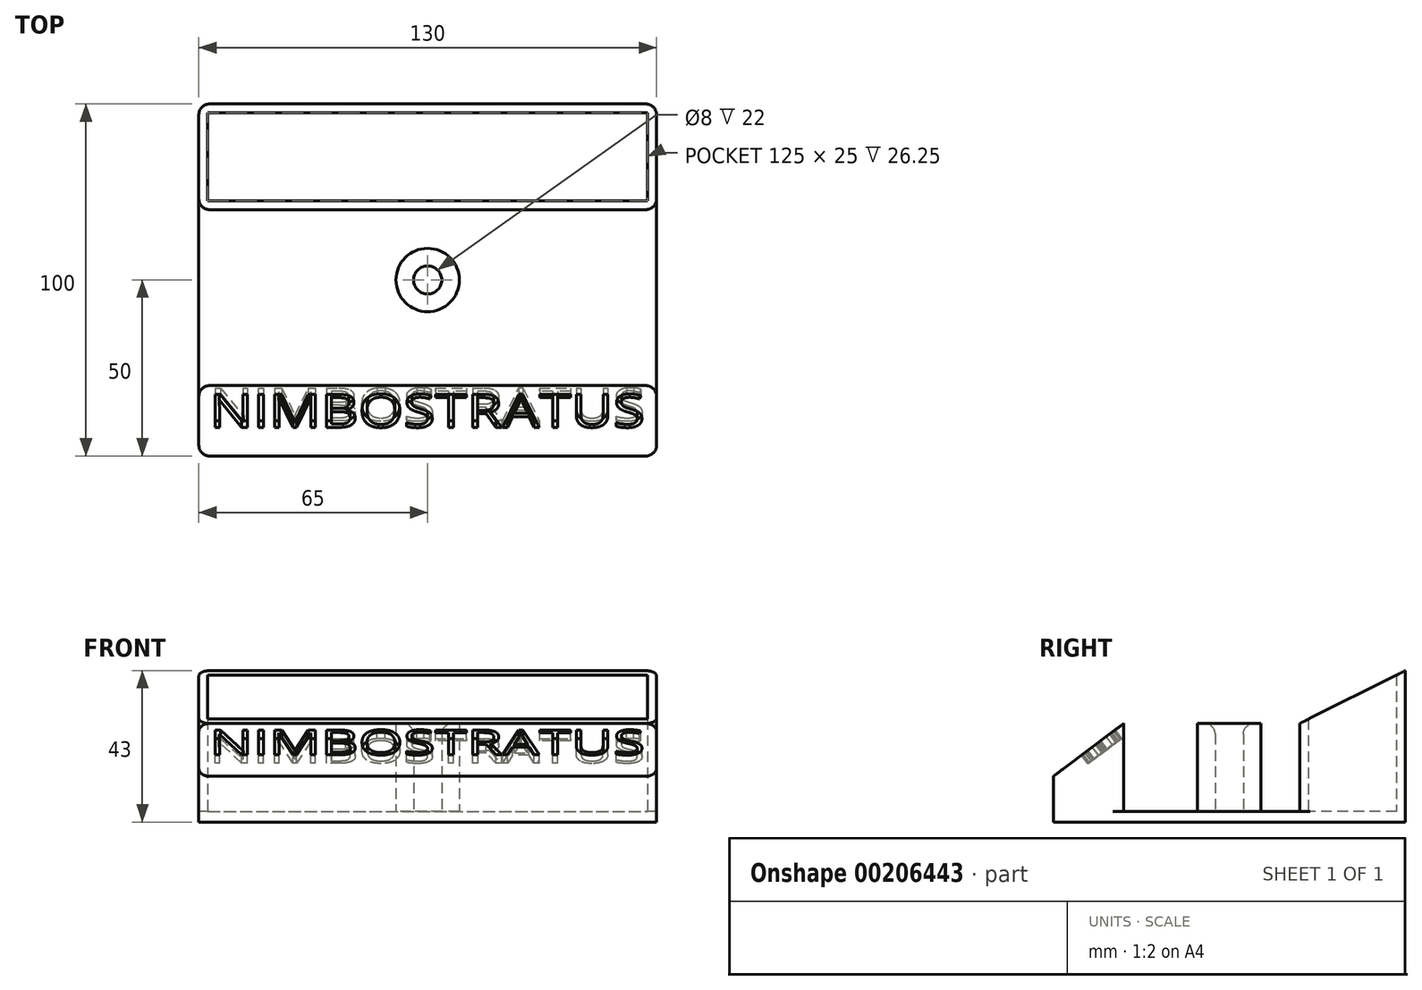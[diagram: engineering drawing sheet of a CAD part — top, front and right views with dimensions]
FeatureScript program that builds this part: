
annotation { "Feature Type Name" : "Feature", "Feature Type Description" : "" }
export const myFeature = defineFeature(function(context is Context, id is Id, definition is map)
    precondition{}
    {
        {
            var Q0;
            Q0=qCreatedBy(makeId("Top.planeOp"),FACE);
            var sketch = newSketch(context, id + "F0", { "sketchPlane" : qUnion([Q0])});
            skLineSegment(sketch, "E0.bottom", {"start": v(-65, 100) * mm, "end": v(65, 100) * mm});
            skLineSegment(sketch, "E0.top", {"start": v(-65, 0) * mm, "end": v(65, 0) * mm});
            skLineSegment(sketch, "E0.left", {"start": v(65, 100) * mm, "end": v(65, 0) * mm});
            skLineSegment(sketch, "E0.right", {"start": v(-65, 100) * mm, "end": v(-65, 0) * mm});
            skSolve(sketch);
        }
        {
            var Q0;
            Q0=makeQuery(id+"F0.imprint","IMPRINT",FACE,{"disambiguationData":[TD([[makeQuery(id+"F0.imprint","IMPRINT",EDGE,{"derivedFrom":sQuery(id+"F0.wireOp",EDGE,"E0.bottom")}),-1.0]])]});
            extrude(context, id + "F1", {"entities" : qUnion([Q0]), "depth" : 3 * mm});
        }
        {
            var Q0;
            Q0=makeQuery(id+"F1.opExtrude","CAP_FACE",FACE,{"disambiguationData":[OSD([sQuery(id+"F0.wireOp",EDGE,"E0.bottom"),sQuery(id+"F0.wireOp",EDGE,"E0.top"),sQuery(id+"F0.wireOp",EDGE,"E0.left"),sQuery(id+"F0.wireOp",EDGE,"E0.right")])],"isStart":false});
            var sketch = newSketch(context, id + "F2", { "sketchPlane" : qUnion([Q0])});
            skLineSegment(sketch, "E1", {"start": v(0, 0) * mm, "end": v(0, 100) * mm, "construction": true});
            skCircle(sketch, "E2", {"center": v(0, 50) * mm, "radius": 9 * mm});
            skCircle(sketch, "E3", {"center": v(0, 50) * mm, "radius": 4 * mm});
            skLineSegment(sketch, "E4.bottom", {"start": v(-65, 0) * mm, "end": v(65, 0) * mm});
            skLineSegment(sketch, "E4.top", {"start": v(-65, 20) * mm, "end": v(65, 20) * mm});
            skLineSegment(sketch, "E4.left", {"start": v(-65, 0) * mm, "end": v(-65, 20) * mm});
            skLineSegment(sketch, "E4.right", {"start": v(65, 0) * mm, "end": v(65, 20) * mm});
            skLineSegment(sketch, "E5.bottom", {"start": v(-65, 100) * mm, "end": v(65, 100) * mm});
            skLineSegment(sketch, "E5.top", {"start": v(-65, 70) * mm, "end": v(65, 70) * mm});
            skLineSegment(sketch, "E5.left", {"start": v(-65, 100) * mm, "end": v(-65, 70) * mm});
            skLineSegment(sketch, "E5.right", {"start": v(65, 100) * mm, "end": v(65, 70) * mm});
            skLineSegment(sketch, "E6.0", {"start": v(62.5, 97.5) * mm, "end": v(62.5, 72.5) * mm});
            skLineSegment(sketch, "E6.1", {"start": v(-62.5, 97.5) * mm, "end": v(62.5, 97.5) * mm});
            skLineSegment(sketch, "E6.2", {"start": v(-62.5, 97.5) * mm, "end": v(-62.5, 72.5) * mm});
            skLineSegment(sketch, "E6.3", {"start": v(-62.5, 72.5) * mm, "end": v(62.5, 72.5) * mm});
            skSolve(sketch);
        }
        {
            var Q0;
            Q0=makeQuery(id+"F2.imprint","IMPRINT",FACE,{"disambiguationData":[TD([[makeQuery(id+"F2.imprint","IMPRINT",EDGE,{"derivedFrom":sQuery(id+"F2.wireOp",EDGE,"E5.bottom")}),-1.0]])]});
            extrude(context, id + "F3", {"entities" : qUnion([Q0]), "operationType" : NewBodyOperationType.ADD, "depth" : 40 * mm});
        }
        {
            var Q0;
            Q0=makeQuery(id+"F2.imprint","IMPRINT",FACE,{"disambiguationData":[TD([[makeQuery(id+"F2.imprint","IMPRINT",EDGE,{"derivedFrom":sQuery(id+"F2.wireOp",EDGE,"E2")}),1.0]])]});
            var Q1;
            Q1=makeQuery(id+"F2.imprint","IMPRINT",FACE,{"disambiguationData":[TD([[makeQuery(id+"F2.imprint","IMPRINT",EDGE,{"derivedFrom":sQuery(id+"F2.wireOp",EDGE,"E4.bottom")}),1.0]])]});
            extrude(context, id + "F4", {"entities" : qUnion([Q0, Q1]), "operationType" : NewBodyOperationType.ADD, "depth" : 25 * mm});
        }
        {
            var Q0;
            Q0=makeQuery(id+"F4.opExtrude","CAP_EDGE",EDGE,{"disambiguationData":[OSD([sQuery(id+"F2.wireOp",EDGE,"E4.bottom")])],"isStart":false});
            chamfer(context, id + "F5", {"entities" : qUnion([Q0]), "chamferType" : ChamferType.TWO_OFFSETS, "width1" : 20 * mm, "oppositeDirection" : false, "width2" : 15 * mm, "tangentPropagation" : true});
        }
        {
            var Q0;
            Q0=makeQuery(id+"F3.opExtrude","CAP_EDGE",EDGE,{"disambiguationData":[OSD([sQuery(id+"F2.wireOp",EDGE,"E5.top")])],"isStart":false});
            chamfer(context, id + "F6", {"entities" : qUnion([Q0]), "chamferType" : ChamferType.TWO_OFFSETS, "width1" : 30 * mm, "oppositeDirection" : false, "width2" : 15 * mm, "tangentPropagation" : true});
        }
        {
            var Q0;
            Q0=makeQuery(id+"F3.boolean.opBoolean","MERGE",EDGE,{"derivedFrom":[makeQuery(id+"F1.opExtrude","SWEPT_EDGE",EDGE,{"disambiguationData":[OSD([sQuery(id+"F0.wireOp",EDGE,"E0.bottom"),sQuery(id+"F0.wireOp",EDGE,"E0.right")])]}),makeQuery(id+"F3.opExtrude","SWEPT_EDGE",EDGE,{"disambiguationData":[OSD([sQuery(id+"F2.wireOp",EDGE,"E5.bottom"),sQuery(id+"F2.wireOp",EDGE,"E5.left")])]})]});
            var Q1;
            Q1=makeQuery(id+"F3.opExtrude","SWEPT_EDGE",EDGE,{"disambiguationData":[OSD([sQuery(id+"F0.wireOp",EDGE,"E0.right"),sQuery(id+"F2.wireOp",EDGE,"E5.top"),sQuery(id+"F2.wireOp",EDGE,"E5.left")])]});
            var Q2;
            Q2=makeQuery(id+"F3.opExtrude","SWEPT_EDGE",EDGE,{"disambiguationData":[OSD([sQuery(id+"F0.wireOp",EDGE,"E0.left"),sQuery(id+"F2.wireOp",EDGE,"E5.top"),sQuery(id+"F2.wireOp",EDGE,"E5.right")])]});
            var Q3;
            Q3=makeQuery(id+"F4.boolean.opBoolean","MERGE",EDGE,{"derivedFrom":[makeQuery(id+"F1.opExtrude","SWEPT_EDGE",EDGE,{"disambiguationData":[OSD([sQuery(id+"F0.wireOp",EDGE,"E0.top"),sQuery(id+"F0.wireOp",EDGE,"E0.right")])]}),makeQuery(id+"F4.opExtrude","SWEPT_EDGE",EDGE,{"disambiguationData":[OSD([sQuery(id+"F2.wireOp",EDGE,"E4.bottom"),sQuery(id+"F2.wireOp",EDGE,"E4.left")])]})]});
            var Q4;
            Q4=makeQuery(id+"F3.boolean.opBoolean","MERGE",EDGE,{"derivedFrom":[makeQuery(id+"F1.opExtrude","SWEPT_EDGE",EDGE,{"disambiguationData":[OSD([sQuery(id+"F0.wireOp",EDGE,"E0.bottom"),sQuery(id+"F0.wireOp",EDGE,"E0.left")])]}),makeQuery(id+"F3.opExtrude","SWEPT_EDGE",EDGE,{"disambiguationData":[OSD([sQuery(id+"F2.wireOp",EDGE,"E5.bottom"),sQuery(id+"F2.wireOp",EDGE,"E5.right")])]})]});
            var Q5;
            Q5=makeQuery(id+"F4.boolean.opBoolean","MERGE",EDGE,{"derivedFrom":[makeQuery(id+"F1.opExtrude","SWEPT_EDGE",EDGE,{"disambiguationData":[OSD([sQuery(id+"F0.wireOp",EDGE,"E0.top"),sQuery(id+"F0.wireOp",EDGE,"E0.left")])]}),makeQuery(id+"F4.opExtrude","SWEPT_EDGE",EDGE,{"disambiguationData":[OSD([sQuery(id+"F2.wireOp",EDGE,"E4.bottom"),sQuery(id+"F2.wireOp",EDGE,"E4.right")])]})]});
            var Q6;
            Q6=makeQuery(id+"F4.opExtrude","SWEPT_EDGE",EDGE,{"disambiguationData":[OSD([sQuery(id+"F0.wireOp",EDGE,"E0.left"),sQuery(id+"F2.wireOp",EDGE,"E4.top"),sQuery(id+"F2.wireOp",EDGE,"E4.right")])]});
            var Q7;
            Q7=makeQuery(id+"F4.opExtrude","SWEPT_EDGE",EDGE,{"disambiguationData":[OSD([sQuery(id+"F0.wireOp",EDGE,"E0.right"),sQuery(id+"F2.wireOp",EDGE,"E4.top"),sQuery(id+"F2.wireOp",EDGE,"E4.left")])]});
            var Q8;
            Q8=makeQuery(id+"F4.opExtrude","CAP_EDGE",EDGE,{"disambiguationData":[OSD([sQuery(id+"F2.wireOp",EDGE,"E3")])],"isStart":false});
            fillet(context, id + "F7", {"entities" : qUnion([Q0, Q1, Q2, Q3, Q4, Q5, Q6, Q7, Q8]), "radius" : 3 * mm, "tangentPropagation" : true, "allowEdgeOverflow" : false});
        }
        {
            var Q0;
            Q0=makeQuery(id+"F5.opChamfer","BLEND_FACE",FACE,{"disambiguationData":[OSD([sQuery(id+"F2.wireOp",EDGE,"E4.bottom")])]});
            var sketch = newSketch(context, id + "F8", { "sketchPlane" : qUnion([Q0])});
            skLineSegment(sketch, "E7.0", {"start": v(62, 10.8) * mm, "end": v(-62, 10.8) * mm});
            skLineSegment(sketch, "E8.0", {"start": v(-62, 29.8) * mm, "end": v(62, 29.8) * mm});
            skText(sketch, "E9", { "text": "NIMBOSTRATUS", "fontName": "OpenSans-Regular.ttf"});
            skLineSegment(sketch, "E10", {"start": v(-62, 10.8) * mm, "end": v(-62, 47.82) * mm});
            skLineSegment(sketch, "E11", {"start": v(62, 10.8) * mm, "end": v(62, 49.07) * mm});
            skPoint(sketch, "E11.endSnap0", {"position": v(62, 15.3) * mm});
            const initialGuessF8  = {"E9": [-0.062, 0.018, 1, 0, 0.0118]};
            skSetInitialGuess(sketch, initialGuessF8);
            skSolve(sketch);
        }
        {
            var Q0;
            Q0=makeQuery(id+"F8.imprint","IMPRINT",FACE,{"disambiguationData":[TD([[makeQuery(id+"F8.imprint","IMPRINT",EDGE,{"derivedFrom":sQuery(id+"F8.wireOp",EDGE,"E9.sketch_text.stroke-0")}),-1.0]])]});
            var Q1;
            Q1=makeQuery(id+"F8.imprint","IMPRINT",FACE,{"disambiguationData":[TD([[makeQuery(id+"F8.imprint","IMPRINT",EDGE,{"derivedFrom":sQuery(id+"F8.wireOp",EDGE,"E9.sketch_text.stroke-13")}),-1.0]])]});
            var Q2;
            Q2=makeQuery(id+"F8.imprint","IMPRINT",FACE,{"disambiguationData":[TD([[makeQuery(id+"F8.imprint","IMPRINT",EDGE,{"derivedFrom":sQuery(id+"F8.wireOp",EDGE,"E9.sketch_text.stroke-19")}),-1.0]])]});
            var Q3;
            Q3=makeQuery(id+"F8.imprint","IMPRINT",FACE,{"disambiguationData":[TD([[makeQuery(id+"F8.imprint","IMPRINT",EDGE,{"derivedFrom":sQuery(id+"F8.wireOp",EDGE,"E9.sketch_text.stroke-27")}),-1.0]])]});
            var Q4;
            Q4=makeQuery(id+"F8.imprint","IMPRINT",FACE,{"disambiguationData":[TD([[makeQuery(id+"F8.imprint","IMPRINT",EDGE,{"derivedFrom":sQuery(id+"F8.wireOp",EDGE,"E9.sketch_text.stroke-43")}),-1.0]])]});
            var Q5;
            Q5=makeQuery(id+"F8.imprint","IMPRINT",FACE,{"disambiguationData":[TD([[makeQuery(id+"F8.imprint","IMPRINT",EDGE,{"derivedFrom":sQuery(id+"F8.wireOp",EDGE,"E9.sketch_text.stroke-58")}),-1.0]])]});
            var Q6;
            Q6=makeQuery(id+"F8.imprint","IMPRINT",FACE,{"disambiguationData":[TD([[makeQuery(id+"F8.imprint","IMPRINT",EDGE,{"derivedFrom":sQuery(id+"F8.wireOp",EDGE,"E9.sketch_text.stroke-72")}),-1.0]])]});
            var Q7;
            Q7=makeQuery(id+"F8.imprint","IMPRINT",FACE,{"disambiguationData":[TD([[makeQuery(id+"F8.imprint","IMPRINT",EDGE,{"derivedFrom":sQuery(id+"F8.wireOp",EDGE,"E9.sketch_text.stroke-90")}),-1.0]])]});
            var Q8;
            Q8=makeQuery(id+"F8.imprint","IMPRINT",FACE,{"disambiguationData":[TD([[makeQuery(id+"F8.imprint","IMPRINT",EDGE,{"derivedFrom":sQuery(id+"F8.wireOp",EDGE,"E9.sketch_text.stroke-104")}),-1.0]])]});
            var Q9;
            Q9=makeQuery(id+"F8.imprint","IMPRINT",FACE,{"disambiguationData":[TD([[makeQuery(id+"F8.imprint","IMPRINT",EDGE,{"derivedFrom":sQuery(id+"F8.wireOp",EDGE,"E9.sketch_text.stroke-110")}),-1.0]])]});
            var Q10;
            Q10=makeQuery(id+"F8.imprint","IMPRINT",FACE,{"disambiguationData":[TD([[makeQuery(id+"F8.imprint","IMPRINT",EDGE,{"derivedFrom":sQuery(id+"F8.wireOp",EDGE,"E9.sketch_text.stroke-124")}),-1.0]])]});
            var Q11;
            Q11=makeQuery(id+"F8.imprint","IMPRINT",FACE,{"disambiguationData":[TD([[makeQuery(id+"F8.imprint","IMPRINT",EDGE,{"derivedFrom":sQuery(id+"F8.wireOp",EDGE,"E9.sketch_text.stroke-15")}),-1.0]])]});
            var Q12;
            Q12=makeQuery(id+"F8.imprint","IMPRINT",FACE,{"disambiguationData":[TD([[makeQuery(id+"F8.imprint","IMPRINT",EDGE,{"derivedFrom":sQuery(id+"F8.wireOp",EDGE,"E9.sketch_text.stroke-129")}),-1.0]])]});
            var Q13;
            Q13=makeQuery(id+"F8.imprint","IMPRINT",FACE,{"disambiguationData":[TD([[makeQuery(id+"F8.imprint","IMPRINT",EDGE,{"derivedFrom":sQuery(id+"F8.wireOp",EDGE,"E9.sketch_text.stroke-142")}),-1.0]])]});
            var Q14;
            Q14=makeQuery(id+"F8.imprint","IMPRINT",FACE,{"disambiguationData":[TD([[makeQuery(id+"F8.imprint","IMPRINT",EDGE,{"derivedFrom":sQuery(id+"F8.wireOp",EDGE,"E9.sketch_text.stroke-150")}),-1.0]])]});
            var Q15;
            Q15=makeQuery(id+"F8.imprint","IMPRINT",FACE,{"disambiguationData":[TD([[makeQuery(id+"F8.imprint","IMPRINT",EDGE,{"derivedFrom":sQuery(id+"F8.wireOp",EDGE,"E9.sketch_text.stroke-164")}),-1.0]])]});
            extrude(context, id + "F9", {"entities" : qUnion([Q0, Q1, Q2, Q3, Q4, Q5, Q6, Q7, Q8, Q9, Q10, Q11, Q12, Q13, Q14, Q15]), "operationType" : NewBodyOperationType.REMOVE, "oppositeDirection" : true, "depth" : 3 * mm});
        }
    });
